# Revit family: Lighting_Recessed-Can
name_source: partatom
category: Lighting Fixtures
units: mm (PartAtom-declared; Revit-internal decimal feet)

## family parameters
Always vertical = Yes
Classification Number = 23.80.70.11
Cut with Voids When Loaded = No
Host = Ceiling
Light Source = Yes
Maintain Annotation Orientation = No
Part Type = Normal
Room Calculation Point = No
Round Connector Dimension = Use Diameter
Shared = No

## types (3) — shared parameters
Assembly Code = D5020220
Baffle Material = ARCAT - Plastic, ABS - Black
Color Filter = 16777215
Construction Details = http://www.arcat.com
Default Elevation = 0' - 0"
Dimming Lamp Color Temperature Shift = <None>
Green Building-LEED = http://www.arcat.com
Housing Material = ARCAT - Metal - Aluminum, Sheet
Keynote = 16510
Lamp = By Family
Light Source Symbol Size = 2' - 0"
Manufacturer = Generic
Manufacturer Fax = (203) 929-2444
Manufacturer Website = http://www.arcat.com
Model = Generic
Product Data = http://www.arcat.com
Product Properties = http://www.arcat.com
Specification = http://www.arcat.com
UL Listed = Yes
Wattage Comments = By Family
zero-valued in all types: Expected Lifespan (Years), Maintenance Schedule (Months), Warranty Duration (Years)

## per-type parameters (varying)
| type | RO rad | Recessed Light Diameter | canOD |
| 6" Recessed Downlight | 0' - 3" | 0' - 6" | 0' - 3 1/8" |
| 5" Recessed Downlight | 0' - 2 1/2" | 0' - 5" | 0' - 2 5/8" |
| 4" Recessed Downlight | 0' - 2" | 0' - 4" | 0' - 2 1/8" |

note: column(s) folded — value = type name in every type: Description

## geometry (parser evidence)
native form markers: Sweep x7
no freeform markers — native parametric forms only
